# Revit family: Plumbing-Pipes-KOHLER-Complementary -K-16407IN
name_source: partatom
category: Plumbing Fixtures
units: mm (PartAtom-declared; Revit-internal decimal feet)

## family parameters
Cut with Voids When Loaded = No
Host = Face
OmniClass Number = 23.31.13.00
OmniClass Title = Sinks
Part Type = Normal
Room Calculation Point = No
Round Connector Dimension = Use Diameter
Shared = No

## types (4) — shared parameters
ADA Compliant = No
Assembly Code = D2010
CW Connection = No
Cold Water Inlet = Cold Water Inlet
Date Modified = 03/05/2023
Default Elevation = 18"
Description = Lavatory Bottle Trap, Without Drain
Drain Included = No
Flow Rate = 0 GPM
HW Connection = No
Hot Water Inlet = Hot Water Inlet
Length = 7 7/16"
Manufacturer = Kohler Co.
Master Format 2014 = 22 41 39
Master Format 2014 Name = Residential Faucets, Supplies, and Trim
Material = Premium Metal Construction
Pressure = 0.00 psi
Product Name = Complementary
URL = https://www.kohler.co.in
Vent Connection = No
Waste Connection = Yes
Waste Water Inlet = Waste Water Inlet
Waste Water Outlet = Waste Water Outlet
WaterSense Certified = No
Width = 2 9/16"

## per-type parameters (varying)
| type | Finish | Model | Product Page URL | Type |
| AF-Vibrant French Gold | Kohler-Metal-AF-Vibrant_French_Gold | K-16407IN-AF |  | 1 |
| BN-Vibrant Brushed Nickel | Kohler-Metal-BN-Vibrant_Brushed_Nickel | K-16407IN-BN |  | 2 |
| BV-Brushed Bronze | Kohler-Metal-BV-Brushed_Bronze | K-16407IN-BV |  | 3 |
| CP-Polished Chrome | Kohler-Metal-CP-Polished_Chrome | K-16407IN-CP | https://www.kohler.co.in | 4 |

## geometry (parser evidence)
native form markers: Sweep x3
no freeform markers — native parametric forms only
